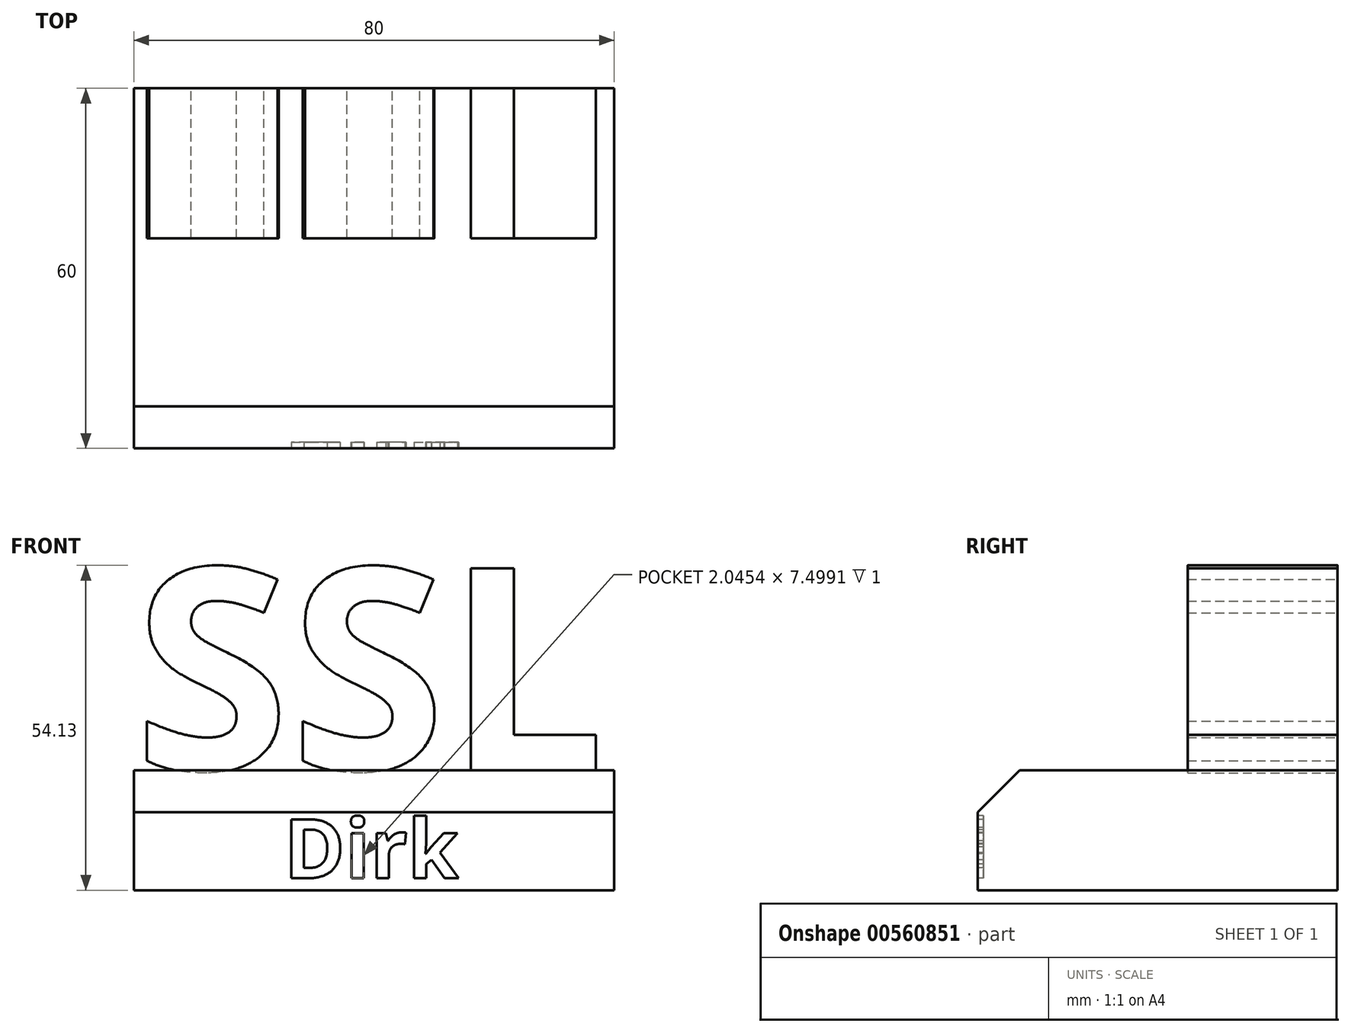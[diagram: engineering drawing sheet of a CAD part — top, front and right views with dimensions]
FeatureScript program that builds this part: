
annotation { "Feature Type Name" : "Feature", "Feature Type Description" : "" }
export const myFeature = defineFeature(function(context is Context, id is Id, definition is map)
    precondition{}
    {
        {
            var Q0;
            Q0=qCreatedBy(makeId("Top.planeOp"),FACE);
            var sketch = newSketch(context, id + "F0", { "sketchPlane" : qUnion([Q0])});
            skLineSegment(sketch, "E0.bottom", {"start": v(40, 0) * mm, "end": v(-40, 0) * mm});
            skLineSegment(sketch, "E0.top", {"start": v(40, -60) * mm, "end": v(-40, -60) * mm});
            skLineSegment(sketch, "E0.left", {"start": v(40, 0) * mm, "end": v(40, -60) * mm});
            skLineSegment(sketch, "E0.right", {"start": v(-40, 0) * mm, "end": v(-40, -60) * mm});
            skPoint(sketch, "E0.middle", {"position": v(0, 0) * mm});
            skSolve(sketch);
        }
        {
            var Q0;
            Q0 = qSketchRegion(id + "F0", true);
            extrude(context, id + "F1", {"entities" : qUnion([Q0]), "depth" : 20 * mm, "offsetDistance" : 25 * mm});
        }
        {
            var Q0;
            Q0=qCreatedBy(makeId("Front.planeOp"),FACE);
            var sketch = newSketch(context, id + "F2", { "sketchPlane" : qUnion([Q0])});
            skText(sketch, "E1", { "text": "SSL", "fontName": "OpenSans-Bold.ttf"});
            const initialGuessF2  = {"E1": [-0.04, 0.02, 1, 0, 0.03394]};
            skSetInitialGuess(sketch, initialGuessF2);
            skSolve(sketch);
        }
        {
            var Q0;
            Q0 = qSketchRegion(id + "F2", true);
            extrude(context, id + "F3", {"entities" : qUnion([Q0]), "depth" : 25 * mm, "offsetDistance" : 25 * mm});
        }
        {
            var Q0;
            Q0=makeQuery(id+"F1.opExtrude","CAP_EDGE",EDGE,{"disambiguationData":[OSD([sQuery(id+"F0.wireOp",EDGE,"E0.top")])],"isStart":false});
            chamfer(context, id + "F4", {"entities" : qUnion([Q0]), "width" : 7 * mm, "tangentPropagation" : true});
        }
        {
            var Q0;
            Q0=makeQuery(id+"F1.opExtrude","SWEPT_FACE",FACE,{"disambiguationData":[OSD([sQuery(id+"F0.wireOp",EDGE,"E0.top")])]});
            var sketch = newSketch(context, id + "F5", { "sketchPlane" : qUnion([Q0])});
            skText(sketch, "E2", { "text": "Dirk", "fontName": "OpenSans-Bold.ttf"});
            const initialGuessF5  = {"E2": [-0.015, 0.002, 1, 0, 0.00989]};
            skSetInitialGuess(sketch, initialGuessF5);
            skSolve(sketch);
        }
        {
            var Q0;
            Q0 = qSketchRegion(id + "F5", true);
            extrude(context, id + "F6", {"entities" : qUnion([Q0]), "operationType" : NewBodyOperationType.REMOVE, "oppositeDirection" : true, "depth" : 1 * mm, "offsetDistance" : 25 * mm});
        }
    });
